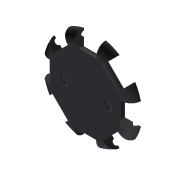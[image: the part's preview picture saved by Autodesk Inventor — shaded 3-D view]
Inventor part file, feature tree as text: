
AUTODESK INVENTOR PART (.ipt)
format: ipt  version: 2017 (Build 210142000, 142)  size: 246,272 bytes
history: native  units: mm
features: sketch x4, extrude x3, projected_geometry x2, revolve x1, fillet x1, pattern_circular x1, hole x1
ambient origin geometry x8: Origin, YZ Plane, XZ Plane, XY Plane, X Axis, Y Axis, Z Axis, Center Point
bodies: Solid1 (feature_tree)
feature tree (13):
  sketch  "Sketch1"  dims[d0=60.0mm d1=14.0mm]
  extrude  "Extrusion1"  Depth=14.0mm
  revolve  "Revolution1"  [1 undecoded]
  extrude  "Extrusion2"  Depth=1.75mm
  fillet  "Fillet1"  Radius=1.75mm
  pattern_circular  "Circular Pattern1"  [2 undecoded]
  hole  "Hole1"  [1 undecoded]
  extrude  "Extrusion3"  Depth=3.0mm TaperAngle=0.0deg
  sketch  "Sketch2"  dims[d2=7.0mm d3=19.0mm]
  projected_geometry  "Projected Loop1"
  sketch  "Sketch3"  dims[d4=5.0mm d5=5.0mm d6=1.75mm]
  sketch  "Sketch4"  dims[d7=1.75mm d8=6.0mm d9=0.0mm d10=90.0deg d11=12.0mm d12=0.0mm d13=6.0mm d14=80.0mm d15=360.0deg d17=14.0mm d18=14.0mm d19=4.0mm d20=6.0mm d21=4.0mm d22=2.0mm d23=90.0deg d24=8.0mm d25=20.594885mm d26=5.5mm d27=5.5mm d28=3.0mm d29=0.0mm]
  projected_geometry  "Projected Loop2"
note: 4 required parameter values undecoded (feature->parameter linkage not recoverable at this tier; creation-order binding heuristic only, values carry confidence <= 0.55)